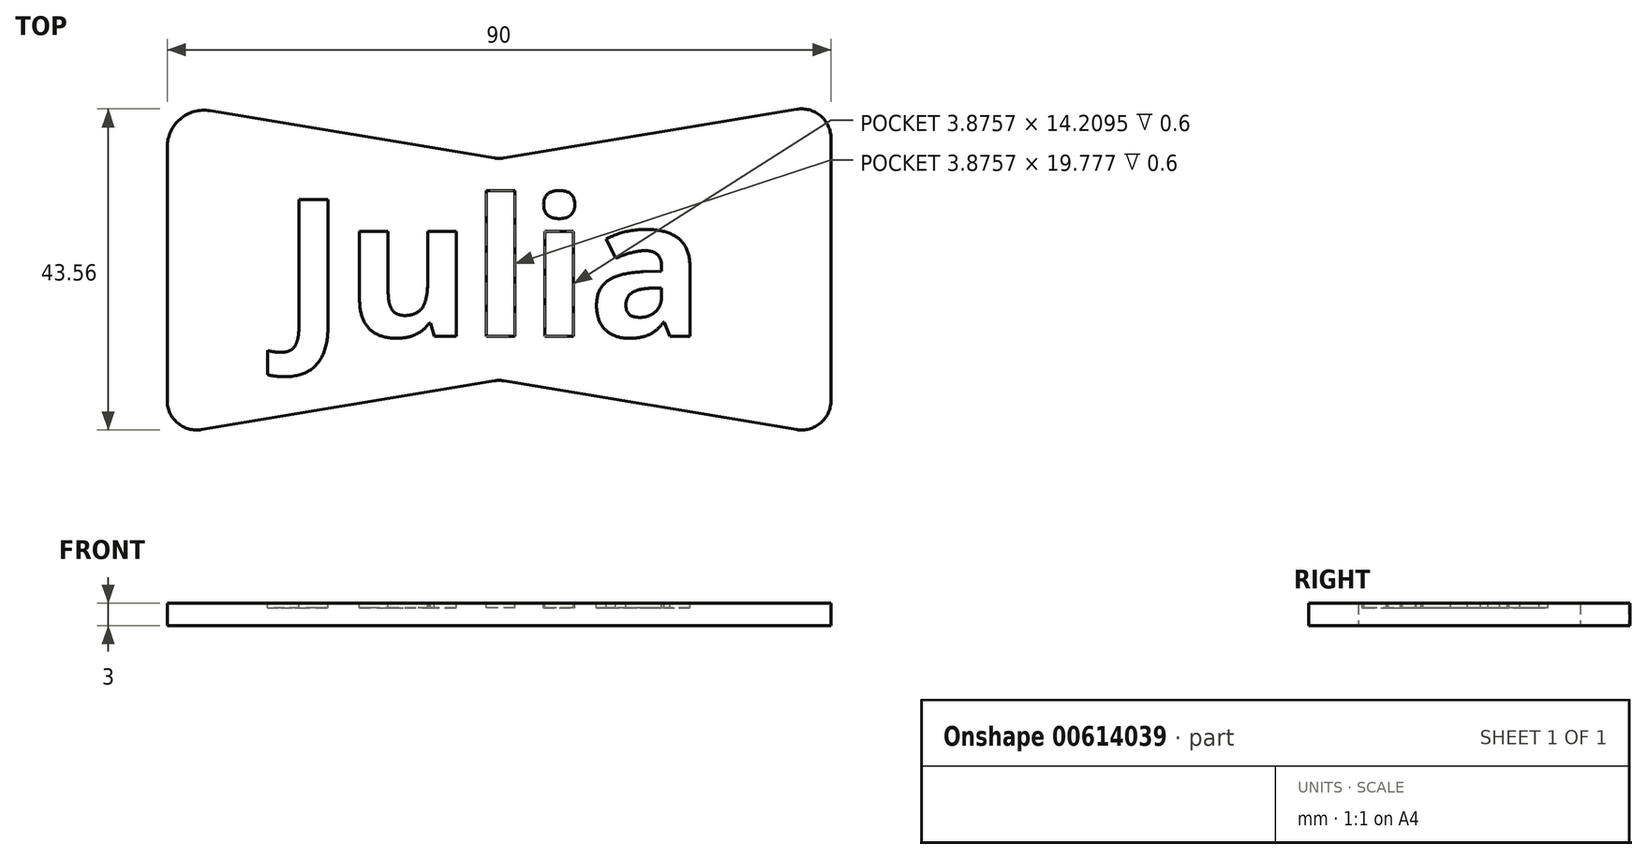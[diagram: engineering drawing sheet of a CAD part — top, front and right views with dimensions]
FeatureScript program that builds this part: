
annotation { "Feature Type Name" : "Feature", "Feature Type Description" : "" }
export const myFeature = defineFeature(function(context is Context, id is Id, definition is map)
    precondition{}
    {
        {
            var Q0;
            Q0=qCreatedBy(makeId("Top.planeOp"),FACE);
            var sketch = newSketch(context, id + "F0", { "sketchPlane" : qUnion([Q0])});
            skLineSegment(sketch, "E0.right", {"start": v(-46.71, 14.28) * mm, "end": v(-46.71, -20.1) * mm});
            skPoint(sketch, "E0.left.start.orphan", {"position": v(43.29, 20.18) * mm});
            skPoint(sketch, "E1", {"position": v(-1.71, 13.69) * mm});
            skLineSegment(sketch, "E2", {"start": v(-40.89, 19.21) * mm, "end": v(-2.37, 12.8) * mm});
            skLineSegment(sketch, "E3", {"start": v(-42.05, -24.04) * mm, "end": v(-2.37, -17.43) * mm});
            skLineSegment(sketch, "E4", {"start": v(-1.71, 12.68) * mm, "end": v(-1.71, -17.32) * mm, "construction": true});
            skLineSegment(sketch, "E5.MirrorCS", {"start": v(43.29, 20.18) * mm, "end": v(43.29, -24.82) * mm});
            skLineSegment(sketch, "E6.MirrorCS", {"start": v(38.63, 19.4) * mm, "end": v(-1.05, 12.8) * mm});
            skLineSegment(sketch, "E7.MirrorCS", {"start": v(38.63, -24.04) * mm, "end": v(-1.05, -17.43) * mm});
            skLineSegment(sketch, "E8.MirrorCS", {"start": v(43.29, 15.46) * mm, "end": v(43.29, -20.1) * mm});
            skPoint(sketch, "E9.visualSharp", {"position": v(-46.71, 20.18) * mm});
            skArc(sketch, "E9.filletArc", {"start": v(-40.89, 19.21) * mm, "mid": v(-44.94, 18.1) * mm, "end": v(-46.71, 14.28) * mm});
            skPoint(sketch, "E10.visualSharp", {"position": v(-46.71, -24.82) * mm});
            skArc(sketch, "E10.filletArc", {"start": v(-46.71, -20.1) * mm, "mid": v(-45.3, -23.15) * mm, "end": v(-42.05, -24.04) * mm});
            skArc(sketch, "E11.filletArc", {"start": v(43.29, 15.46) * mm, "mid": v(41.87, 18.51) * mm, "end": v(38.63, 19.4) * mm});
            skPoint(sketch, "E12.visualSharp", {"position": v(43.29, -24.82) * mm});
            skArc(sketch, "E12.filletArc", {"start": v(38.63, -24.04) * mm, "mid": v(41.87, -23.15) * mm, "end": v(43.29, -20.1) * mm});
            skPoint(sketch, "E13.visualSharp", {"position": v(-1.71, -17.32) * mm});
            skArc(sketch, "E13.filletArc", {"start": v(-1.05, -17.43) * mm, "mid": v(-1.71, -17.37) * mm, "end": v(-2.37, -17.43) * mm});
            skPoint(sketch, "E14.visualSharp", {"position": v(-1.71, 12.68) * mm});
            skArc(sketch, "E14.filletArc", {"start": v(-2.37, 12.8) * mm, "mid": v(-1.71, 12.74) * mm, "end": v(-1.05, 12.8) * mm});
            skSolve(sketch);
        }
        {
            var Q0;
            Q0 = qSketchRegion(id + "F0", true);
            extrude(context, id + "F1", {"entities" : qUnion([Q0]), "depth" : 3 * mm, "offsetDistance" : 25 * mm});
        }
        {
            var Q0;
            Q0=makeQuery(id+"F1.opExtrude","CAP_FACE",FACE,{"disambiguationData":[OSD([sQuery(id+"F0.wireOp",EDGE,"E0.right"),sQuery(id+"F0.wireOp",EDGE,"E2"),sQuery(id+"F0.wireOp",EDGE,"E3"),sQuery(id+"F0.wireOp",EDGE,"E6.MirrorCS"),sQuery(id+"F0.wireOp",EDGE,"E7.MirrorCS"),sQuery(id+"F0.wireOp",EDGE,"E8.MirrorCS"),sQuery(id+"F0.wireOp",EDGE,"E9.filletArc"),sQuery(id+"F0.wireOp",EDGE,"E10.filletArc"),sQuery(id+"F0.wireOp",EDGE,"E11.filletArc"),sQuery(id+"F0.wireOp",EDGE,"E12.filletArc"),sQuery(id+"F0.wireOp",EDGE,"E13.filletArc"),sQuery(id+"F0.wireOp",EDGE,"E14.filletArc")])],"isStart":false});
            var sketch = newSketch(context, id + "F2", { "sketchPlane" : qUnion([Q0])});
            skText(sketch, "E15", { "text": "Julia", "fontName": "OpenSans-Bold.ttf"});
            skLineSegment(sketch, "E16", {"start": v(-31.2, -2.04) * mm, "end": v(-46.71, -2.04) * mm, "construction": true});
            skLineSegment(sketch, "E17", {"start": v(27.79, -2.04) * mm, "end": v(43.29, -2.04) * mm, "construction": true});
            const initialGuessF2  = {"E15": [-0.0312, -0.0114, 1, 0, 0.01874]};
            skSetInitialGuess(sketch, initialGuessF2);
            skSolve(sketch);
        }
        {
            var Q0;
            Q0 = qSketchRegion(id + "F2", true);
            extrude(context, id + "F3", {"entities" : qUnion([Q0]), "operationType" : NewBodyOperationType.REMOVE, "oppositeDirection" : true, "depth" : 0.6 * mm, "offsetDistance" : 25 * mm});
        }
    });
